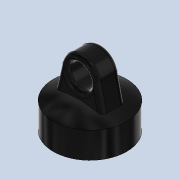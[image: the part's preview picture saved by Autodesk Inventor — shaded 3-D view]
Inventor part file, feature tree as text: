
AUTODESK INVENTOR PART (.ipt)
format: ipt  version: 2020 (Build 240168000, 168)  size: 202,240 bytes
history: native  units: mm
features: sketch x4, extrude x3, other x1, revolve x1, fillet x1
ambient origin geometry x8: Origin, YZ Plane, XZ Plane, XY Plane, X Axis, Y Axis, Z Axis, Center Point
bodies: Body1 (feature_tree), Body2 (feature_tree)
feature tree (10):
  other  "ソリッド1"
  extrude  "押し出し1"  Depth=15.75mm
  extrude  "押し出し2"  Depth=5.6mm TaperAngle=0.0deg
  revolve  "回転1"
  extrude  "押し出し3"  Depth=5.0mm
  fillet  "フィレット1"  Radius=1.5mm
  sketch  "スケッチ1"
  sketch  "スケッチ2"
  sketch  "スケッチ3"
  sketch  "スケッチ4"
